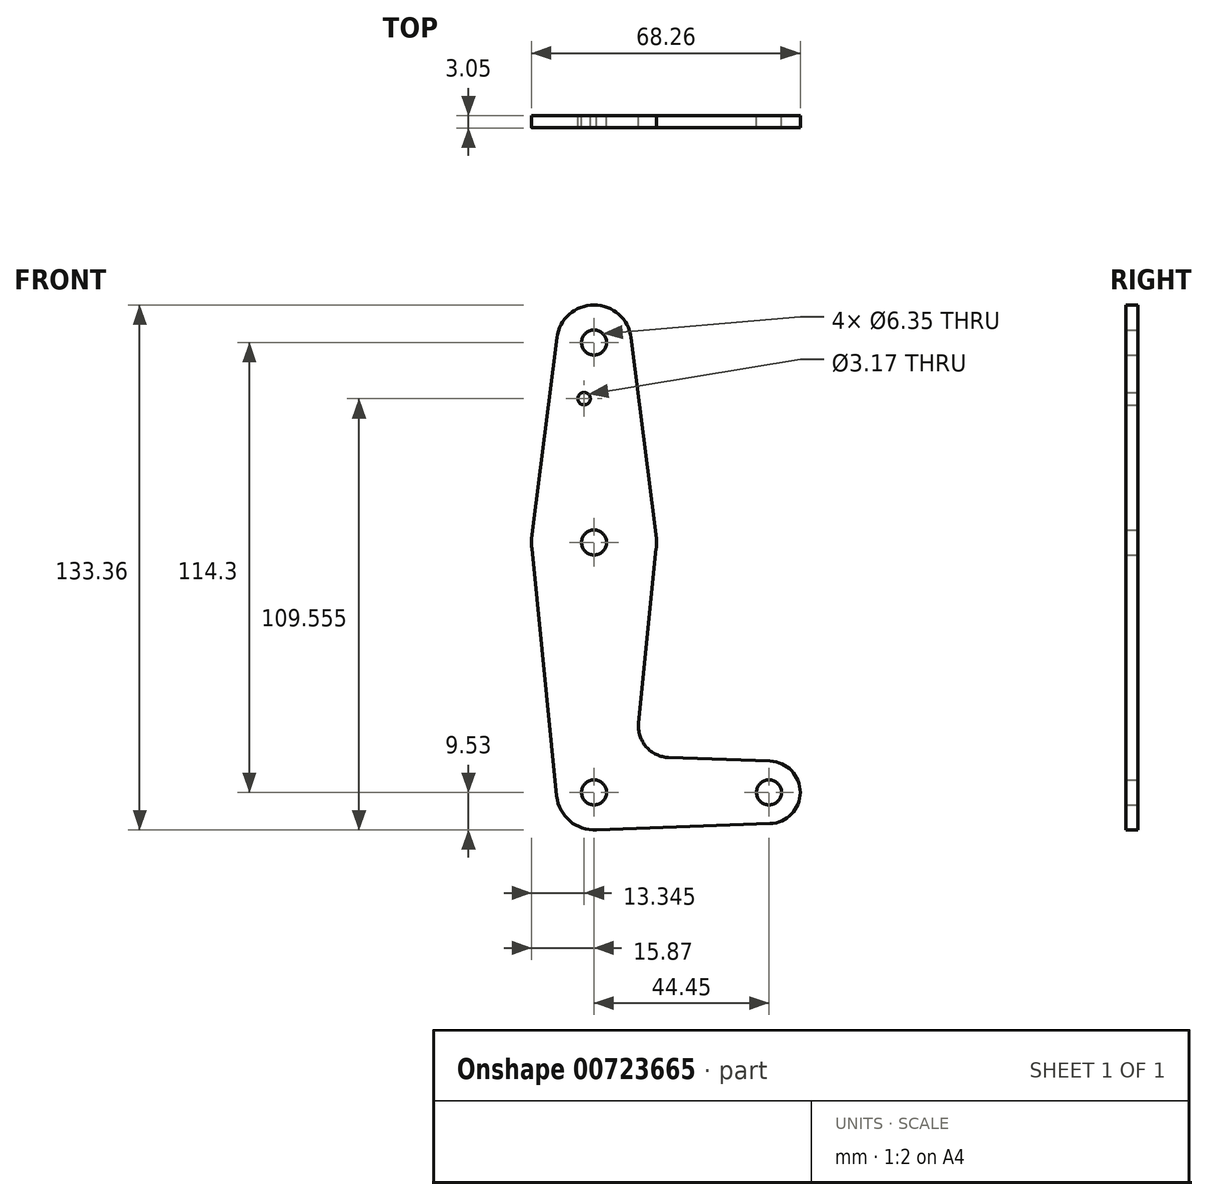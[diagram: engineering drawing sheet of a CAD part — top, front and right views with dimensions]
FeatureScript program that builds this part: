
annotation { "Feature Type Name" : "Feature", "Feature Type Description" : "" }
export const myFeature = defineFeature(function(context is Context, id is Id, definition is map)
    precondition{}
    {
        {
            var Q0;
            Q0=qCreatedBy(makeId("Front.planeOp"),FACE);
            var sketch = newSketch(context, id + "F0", { "sketchPlane" : qUnion([Q0])});
            skLineSegment(sketch, "E0", {"start": v(0, 0) * mm, "end": v(0, 114.3) * mm, "construction": true});
            skLineSegment(sketch, "E1", {"start": v(0, 0) * mm, "end": v(44.45, 0) * mm, "construction": true});
            skCircle(sketch, "E2", {"center": v(0, 0) * mm, "radius": 9.53 * mm});
            skCircle(sketch, "E3", {"center": v(44.45, 0) * mm, "radius": 7.94 * mm});
            skCircle(sketch, "E4", {"center": v(0, 114.3) * mm, "radius": 9.53 * mm});
            skCircle(sketch, "E5", {"center": v(0, 63.5) * mm, "radius": 15.88 * mm});
            skLineSegment(sketch, "E6", {"start": v(-9.45, 115.5) * mm, "end": v(-15.75, 65.48) * mm});
            skLineSegment(sketch, "E7", {"start": v(9.45, 115.5) * mm, "end": v(15.75, 65.48) * mm});
            skLineSegment(sketch, "E8", {"start": v(0, -9.53) * mm, "end": v(44.73, -7.93) * mm});
            skLineSegment(sketch, "E9", {"start": v(44.73, 7.93) * mm, "end": v(18.97, 8.85) * mm});
            skCircle(sketch, "E10", {"center": v(0, 63.5) * mm, "radius": 3.18 * mm});
            skCircle(sketch, "E11", {"center": v(0, 114.3) * mm, "radius": 3.18 * mm});
            skCircle(sketch, "E12", {"center": v(0, 0) * mm, "radius": 3.18 * mm});
            skCircle(sketch, "E13", {"center": v(44.45, 0) * mm, "radius": 3.18 * mm});
            skCircle(sketch, "E14", {"center": v(-2.52, 100.03) * mm, "radius": 1.59 * mm});
            skLineSegment(sketch, "E15", {"start": v(-15.8, 61.91) * mm, "end": v(-9.48, -0.95) * mm});
            skLineSegment(sketch, "E16", {"start": v(15.8, 61.91) * mm, "end": v(11.34, 17.59) * mm});
            skArc(sketch, "E17.filletArc", {"start": v(11.34, 17.59) * mm, "mid": v(13.26, 11.57) * mm, "end": v(18.97, 8.85) * mm});
            skSolve(sketch);
        }
        {
            var Q0;
            Q0 = qSketchRegion(id + "F0", true);
            extrude(context, id + "F1", {"entities" : qUnion([Q0]), "depth" : 3.05 * mm, "offsetDistance" : 25.4 * mm});
        }
    });
